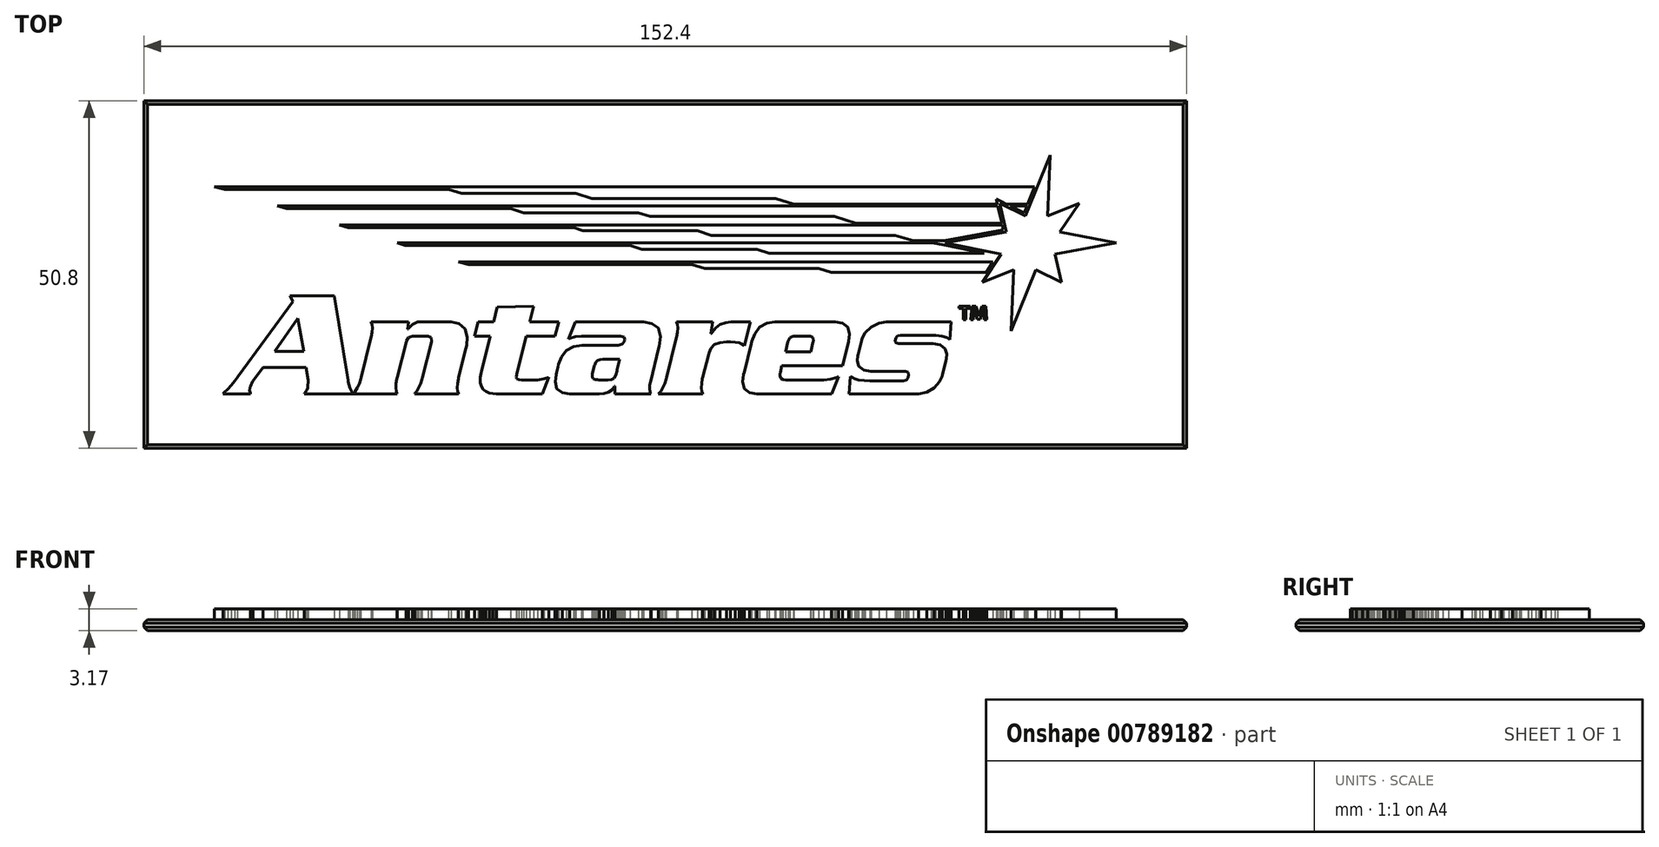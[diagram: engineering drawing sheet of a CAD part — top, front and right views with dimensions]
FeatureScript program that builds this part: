
annotation { "Feature Type Name" : "Feature", "Feature Type Description" : "" }
export const myFeature = defineFeature(function(context is Context, id is Id, definition is map)
    precondition{}
    {
        {
            var Q0;
            Q0=qCreatedBy(makeId("Top.planeOp"),FACE);
            var sketch = newSketch(context, id + "F0", { "sketchPlane" : qUnion([Q0])});
            skLineSegment(sketch, "E0.bottom", {"start": v(76.2, -25.4) * mm, "end": v(-76.2, -25.4) * mm});
            skLineSegment(sketch, "E0.top", {"start": v(76.2, 25.4) * mm, "end": v(-76.2, 25.4) * mm});
            skLineSegment(sketch, "E0.left", {"start": v(76.2, -25.4) * mm, "end": v(76.2, 25.4) * mm});
            skLineSegment(sketch, "E0.right", {"start": v(-76.2, -25.4) * mm, "end": v(-76.2, 25.4) * mm});
            skPoint(sketch, "E0.middle", {"position": v(0, 0) * mm});
            skSolve(sketch);
        }
        {
            var Q0;
            Q0 = qSketchRegion(id + "F0", true);
            extrude(context, id + "F1", {"entities" : qUnion([Q0]), "depth" : 1.59 * mm, "offsetDistance" : 25.4 * mm});
        }
        {
            var Q0;
            Q0=makeQuery(id+"F1.opExtrude","CAP_FACE",FACE,{"disambiguationData":[OSD([sQuery(id+"F0.wireOp",EDGE,"E0.bottom"),sQuery(id+"F0.wireOp",EDGE,"E0.top"),sQuery(id+"F0.wireOp",EDGE,"E0.left"),sQuery(id+"F0.wireOp",EDGE,"E0.right")])],"isStart":false});
            var sketch = newSketch(context, id + "F2", { "sketchPlane" : qUnion([Q0])});
            skLineSegment(sketch, "E1", {"start": v(-52.86, -11.24) * mm, "end": v(-53.7, -6.4) * mm});
            skLineSegment(sketch, "E2", {"start": v(-53.7, -6.4) * mm, "end": v(-57.1, -11.24) * mm});
            skLineSegment(sketch, "E3", {"start": v(-57.1, -11.24) * mm, "end": v(-52.86, -11.24) * mm});
            skLineSegment(sketch, "E4", {"start": v(-58.8, -13.61) * mm, "end": v(-60.26, -15.59) * mm});
            skLineSegment(sketch, "E5", {"start": v(-60.26, -15.59) * mm, "end": v(-60.31, -15.65) * mm});
            skLineSegment(sketch, "E6", {"start": v(-60.31, -15.65) * mm, "end": v(-60.66, -16.36) * mm});
            skLineSegment(sketch, "E7", {"start": v(-60.66, -16.36) * mm, "end": v(-60.68, -16.44) * mm});
            skLineSegment(sketch, "E8", {"start": v(-60.68, -16.44) * mm, "end": v(-60.7, -16.56) * mm});
            skLineSegment(sketch, "E9", {"start": v(-60.7, -16.56) * mm, "end": v(-60.76, -16.95) * mm});
            skLineSegment(sketch, "E10", {"start": v(-60.76, -16.95) * mm, "end": v(-60.66, -17.34) * mm});
            skLineSegment(sketch, "E11", {"start": v(-60.66, -17.34) * mm, "end": v(-60.62, -17.47) * mm});
            skLineSegment(sketch, "E12", {"start": v(-60.62, -17.47) * mm, "end": v(-64.68, -17.47) * mm});
            skLineSegment(sketch, "E13", {"start": v(-64.68, -17.47) * mm, "end": v(-64.5, -17.3) * mm});
            skLineSegment(sketch, "E14", {"start": v(-64.5, -17.3) * mm, "end": v(-63.96, -16.75) * mm});
            skLineSegment(sketch, "E15", {"start": v(-63.96, -16.75) * mm, "end": v(-63.4, -16.17) * mm});
            skLineSegment(sketch, "E16", {"start": v(-63.4, -16.17) * mm, "end": v(-62.92, -15.58) * mm});
            skLineSegment(sketch, "E17", {"start": v(-62.92, -15.58) * mm, "end": v(-62.52, -15.05) * mm});
            skLineSegment(sketch, "E18", {"start": v(-62.52, -15.05) * mm, "end": v(-62.4, -14.87) * mm});
            skLineSegment(sketch, "E19", {"start": v(-62.4, -14.87) * mm, "end": v(-54.45, -3.94) * mm});
            skLineSegment(sketch, "E20", {"start": v(-54.45, -3.94) * mm, "end": v(-54.87, -3.13) * mm});
            skLineSegment(sketch, "E21", {"start": v(-54.87, -3.13) * mm, "end": v(-48.4, -3.13) * mm});
            skLineSegment(sketch, "E22", {"start": v(-48.4, -3.13) * mm, "end": v(-46.37, -15.5) * mm});
            skLineSegment(sketch, "E23", {"start": v(-46.37, -15.5) * mm, "end": v(-46.34, -15.68) * mm});
            skLineSegment(sketch, "E24", {"start": v(-46.34, -15.68) * mm, "end": v(-46.08, -16.56) * mm});
            skLineSegment(sketch, "E25", {"start": v(-46.08, -16.56) * mm, "end": v(-45.7, -17.33) * mm});
            skLineSegment(sketch, "E26", {"start": v(-45.7, -17.33) * mm, "end": v(-45.61, -17.47) * mm});
            skLineSegment(sketch, "E27", {"start": v(-45.61, -17.47) * mm, "end": v(-52.8, -17.47) * mm});
            skLineSegment(sketch, "E28", {"start": v(-52.8, -17.47) * mm, "end": v(-52.7, -17.33) * mm});
            skLineSegment(sketch, "E29", {"start": v(-52.7, -17.33) * mm, "end": v(-52.4, -16.91) * mm});
            skLineSegment(sketch, "E30", {"start": v(-52.4, -16.91) * mm, "end": v(-52.27, -16.6) * mm});
            skLineSegment(sketch, "E31", {"start": v(-52.27, -16.6) * mm, "end": v(-52.25, -16.53) * mm});
            skLineSegment(sketch, "E32", {"start": v(-52.25, -16.53) * mm, "end": v(-52.23, -16.44) * mm});
            skLineSegment(sketch, "E33", {"start": v(-52.23, -16.44) * mm, "end": v(-52.17, -15.53) * mm});
            skLineSegment(sketch, "E34", {"start": v(-52.17, -15.53) * mm, "end": v(-52.19, -15.45) * mm});
            skLineSegment(sketch, "E35", {"start": v(-52.19, -15.45) * mm, "end": v(-52.51, -13.61) * mm});
            skLineSegment(sketch, "E36", {"start": v(-52.51, -13.61) * mm, "end": v(-58.8, -13.61) * mm});
            skLineSegment(sketch, "E37", {"start": v(-37.54, -6.94) * mm, "end": v(-37.66, -8.04) * mm});
            skLineSegment(sketch, "E38", {"start": v(-37.66, -8.04) * mm, "end": v(-37.61, -8.04) * mm});
            skLineSegment(sketch, "E39", {"start": v(-37.61, -8.04) * mm, "end": v(-37.52, -7.9) * mm});
            skLineSegment(sketch, "E40", {"start": v(-37.52, -7.9) * mm, "end": v(-36.95, -7.28) * mm});
            skLineSegment(sketch, "E41", {"start": v(-36.95, -7.28) * mm, "end": v(-36.22, -6.94) * mm});
            skLineSegment(sketch, "E42", {"start": v(-36.22, -6.94) * mm, "end": v(-35.97, -6.94) * mm});
            skLineSegment(sketch, "E43", {"start": v(-35.97, -6.94) * mm, "end": v(-31.7, -6.94) * mm});
            skLineSegment(sketch, "E44", {"start": v(-31.7, -6.94) * mm, "end": v(-31.31, -6.94) * mm});
            skLineSegment(sketch, "E45", {"start": v(-31.31, -6.94) * mm, "end": v(-30.16, -7.2) * mm});
            skLineSegment(sketch, "E46", {"start": v(-30.16, -7.2) * mm, "end": v(-29.26, -7.97) * mm});
            skLineSegment(sketch, "E47", {"start": v(-29.26, -7.97) * mm, "end": v(-28.94, -9.18) * mm});
            skLineSegment(sketch, "E48", {"start": v(-28.94, -9.18) * mm, "end": v(-29.04, -10.38) * mm});
            skLineSegment(sketch, "E49", {"start": v(-29.04, -10.38) * mm, "end": v(-29.13, -10.77) * mm});
            skLineSegment(sketch, "E50", {"start": v(-29.13, -10.77) * mm, "end": v(-30.2, -15.05) * mm});
            skLineSegment(sketch, "E51", {"start": v(-30.2, -15.05) * mm, "end": v(-30.26, -15.27) * mm});
            skLineSegment(sketch, "E52", {"start": v(-30.26, -15.27) * mm, "end": v(-30.38, -15.97) * mm});
            skLineSegment(sketch, "E53", {"start": v(-30.38, -15.97) * mm, "end": v(-30.41, -16.6) * mm});
            skLineSegment(sketch, "E54", {"start": v(-30.41, -16.6) * mm, "end": v(-30.35, -17.07) * mm});
            skLineSegment(sketch, "E55", {"start": v(-30.35, -17.07) * mm, "end": v(-30.25, -17.37) * mm});
            skLineSegment(sketch, "E56", {"start": v(-30.25, -17.37) * mm, "end": v(-30.22, -17.47) * mm});
            skLineSegment(sketch, "E57", {"start": v(-30.22, -17.47) * mm, "end": v(-36.67, -17.47) * mm});
            skLineSegment(sketch, "E58", {"start": v(-36.67, -17.47) * mm, "end": v(-36.6, -17.37) * mm});
            skLineSegment(sketch, "E59", {"start": v(-36.6, -17.37) * mm, "end": v(-36.35, -17.07) * mm});
            skLineSegment(sketch, "E60", {"start": v(-36.35, -17.07) * mm, "end": v(-36.05, -16.6) * mm});
            skLineSegment(sketch, "E61", {"start": v(-36.05, -16.6) * mm, "end": v(-35.76, -15.97) * mm});
            skLineSegment(sketch, "E62", {"start": v(-35.76, -15.97) * mm, "end": v(-35.55, -15.28) * mm});
            skLineSegment(sketch, "E63", {"start": v(-35.55, -15.28) * mm, "end": v(-35.49, -15.05) * mm});
            skLineSegment(sketch, "E64", {"start": v(-35.49, -15.05) * mm, "end": v(-34.2, -9.87) * mm});
            skLineSegment(sketch, "E65", {"start": v(-34.2, -9.87) * mm, "end": v(-34.16, -9.71) * mm});
            skLineSegment(sketch, "E66", {"start": v(-34.16, -9.71) * mm, "end": v(-34.22, -9.2) * mm});
            skLineSegment(sketch, "E67", {"start": v(-34.22, -9.2) * mm, "end": v(-34.7, -9) * mm});
            skLineSegment(sketch, "E68", {"start": v(-34.7, -9) * mm, "end": v(-34.85, -9) * mm});
            skLineSegment(sketch, "E69", {"start": v(-34.85, -9) * mm, "end": v(-36.78, -9) * mm});
            skLineSegment(sketch, "E70", {"start": v(-36.78, -9) * mm, "end": v(-36.96, -9) * mm});
            skLineSegment(sketch, "E71", {"start": v(-36.96, -9) * mm, "end": v(-37.5, -9.2) * mm});
            skLineSegment(sketch, "E72", {"start": v(-37.5, -9.2) * mm, "end": v(-37.83, -9.71) * mm});
            skLineSegment(sketch, "E73", {"start": v(-37.83, -9.71) * mm, "end": v(-37.87, -9.87) * mm});
            skLineSegment(sketch, "E74", {"start": v(-37.87, -9.87) * mm, "end": v(-39.16, -15.05) * mm});
            skLineSegment(sketch, "E75", {"start": v(-39.16, -15.05) * mm, "end": v(-39.22, -15.27) * mm});
            skLineSegment(sketch, "E76", {"start": v(-39.22, -15.27) * mm, "end": v(-39.34, -15.97) * mm});
            skLineSegment(sketch, "E77", {"start": v(-39.34, -15.97) * mm, "end": v(-39.38, -16.6) * mm});
            skLineSegment(sketch, "E78", {"start": v(-39.38, -16.6) * mm, "end": v(-39.3, -17.07) * mm});
            skLineSegment(sketch, "E79", {"start": v(-39.3, -17.07) * mm, "end": v(-39.22, -17.37) * mm});
            skLineSegment(sketch, "E80", {"start": v(-39.22, -17.37) * mm, "end": v(-39.18, -17.47) * mm});
            skLineSegment(sketch, "E81", {"start": v(-39.18, -17.47) * mm, "end": v(-45.64, -17.47) * mm});
            skLineSegment(sketch, "E82", {"start": v(-45.64, -17.47) * mm, "end": v(-45.55, -17.37) * mm});
            skLineSegment(sketch, "E83", {"start": v(-45.55, -17.37) * mm, "end": v(-45.31, -17.07) * mm});
            skLineSegment(sketch, "E84", {"start": v(-45.31, -17.07) * mm, "end": v(-45.01, -16.6) * mm});
            skLineSegment(sketch, "E85", {"start": v(-45.01, -16.6) * mm, "end": v(-44.72, -15.97) * mm});
            skLineSegment(sketch, "E86", {"start": v(-44.72, -15.97) * mm, "end": v(-44.5, -15.28) * mm});
            skLineSegment(sketch, "E87", {"start": v(-44.5, -15.28) * mm, "end": v(-44.45, -15.05) * mm});
            skLineSegment(sketch, "E88", {"start": v(-44.45, -15.05) * mm, "end": v(-43.03, -9.36) * mm});
            skLineSegment(sketch, "E89", {"start": v(-43.03, -9.36) * mm, "end": v(-42.97, -9.13) * mm});
            skLineSegment(sketch, "E90", {"start": v(-42.97, -9.13) * mm, "end": v(-42.85, -8.44) * mm});
            skLineSegment(sketch, "E91", {"start": v(-42.85, -8.44) * mm, "end": v(-42.82, -7.8) * mm});
            skLineSegment(sketch, "E92", {"start": v(-42.82, -7.8) * mm, "end": v(-42.89, -7.34) * mm});
            skLineSegment(sketch, "E93", {"start": v(-42.89, -7.34) * mm, "end": v(-42.98, -7.04) * mm});
            skLineSegment(sketch, "E94", {"start": v(-42.98, -7.04) * mm, "end": v(-43, -6.94) * mm});
            skLineSegment(sketch, "E95", {"start": v(-43, -6.94) * mm, "end": v(-37.54, -6.94) * mm});
            skLineSegment(sketch, "E96", {"start": v(-24.55, -4.79) * mm, "end": v(-19.23, -4.65) * mm});
            skLineSegment(sketch, "E97", {"start": v(-19.23, -4.65) * mm, "end": v(-19.8, -6.94) * mm});
            skLineSegment(sketch, "E98", {"start": v(-19.8, -6.94) * mm, "end": v(-15.59, -6.94) * mm});
            skLineSegment(sketch, "E99", {"start": v(-15.59, -6.94) * mm, "end": v(-16.1, -9) * mm});
            skLineSegment(sketch, "E100", {"start": v(-16.1, -9) * mm, "end": v(-20.31, -9) * mm});
            skLineSegment(sketch, "E101", {"start": v(-20.31, -9) * mm, "end": v(-21.7, -14.56) * mm});
            skLineSegment(sketch, "E102", {"start": v(-21.7, -14.56) * mm, "end": v(-21.72, -14.66) * mm});
            skLineSegment(sketch, "E103", {"start": v(-21.72, -14.66) * mm, "end": v(-21.77, -14.97) * mm});
            skLineSegment(sketch, "E104", {"start": v(-21.77, -14.97) * mm, "end": v(-21.7, -15.23) * mm});
            skLineSegment(sketch, "E105", {"start": v(-21.7, -15.23) * mm, "end": v(-21.41, -15.37) * mm});
            skLineSegment(sketch, "E106", {"start": v(-21.41, -15.37) * mm, "end": v(-21, -15.4) * mm});
            skLineSegment(sketch, "E107", {"start": v(-21, -15.4) * mm, "end": v(-20.86, -15.4) * mm});
            skLineSegment(sketch, "E108", {"start": v(-20.86, -15.4) * mm, "end": v(-19, -15.4) * mm});
            skLineSegment(sketch, "E109", {"start": v(-19, -15.4) * mm, "end": v(-18.68, -15.4) * mm});
            skLineSegment(sketch, "E110", {"start": v(-18.68, -15.4) * mm, "end": v(-17.71, -15.25) * mm});
            skLineSegment(sketch, "E111", {"start": v(-17.71, -15.25) * mm, "end": v(-17.06, -15.03) * mm});
            skLineSegment(sketch, "E112", {"start": v(-17.06, -15.03) * mm, "end": v(-17, -15) * mm});
            skLineSegment(sketch, "E113", {"start": v(-17, -15) * mm, "end": v(-17.94, -17.47) * mm});
            skLineSegment(sketch, "E114", {"start": v(-17.94, -17.47) * mm, "end": v(-24.58, -17.47) * mm});
            skLineSegment(sketch, "E115", {"start": v(-24.58, -17.47) * mm, "end": v(-24.73, -17.47) * mm});
            skLineSegment(sketch, "E116", {"start": v(-24.73, -17.47) * mm, "end": v(-25.19, -17.43) * mm});
            skLineSegment(sketch, "E117", {"start": v(-25.19, -17.43) * mm, "end": v(-25.74, -17.32) * mm});
            skLineSegment(sketch, "E118", {"start": v(-25.74, -17.32) * mm, "end": v(-26.22, -17.12) * mm});
            skLineSegment(sketch, "E119", {"start": v(-26.22, -17.12) * mm, "end": v(-26.6, -16.8) * mm});
            skLineSegment(sketch, "E120", {"start": v(-26.6, -16.8) * mm, "end": v(-26.89, -16.37) * mm});
            skLineSegment(sketch, "E121", {"start": v(-26.89, -16.37) * mm, "end": v(-27.04, -15.8) * mm});
            skLineSegment(sketch, "E122", {"start": v(-27.04, -15.8) * mm, "end": v(-27.05, -15.07) * mm});
            skLineSegment(sketch, "E123", {"start": v(-27.05, -15.07) * mm, "end": v(-26.95, -14.4) * mm});
            skLineSegment(sketch, "E124", {"start": v(-26.95, -14.4) * mm, "end": v(-26.9, -14.18) * mm});
            skLineSegment(sketch, "E125", {"start": v(-26.9, -14.18) * mm, "end": v(-25.6, -9) * mm});
            skLineSegment(sketch, "E126", {"start": v(-25.6, -9) * mm, "end": v(-27.86, -9) * mm});
            skLineSegment(sketch, "E127", {"start": v(-27.86, -9) * mm, "end": v(-27.35, -6.94) * mm});
            skLineSegment(sketch, "E128", {"start": v(-27.35, -6.94) * mm, "end": v(-25.09, -6.94) * mm});
            skLineSegment(sketch, "E129", {"start": v(-25.09, -6.94) * mm, "end": v(-24.55, -4.79) * mm});
            skLineSegment(sketch, "E130", {"start": v(-9, -12.4) * mm, "end": v(-9.13, -12.4) * mm});
            skLineSegment(sketch, "E131", {"start": v(-9.13, -12.4) * mm, "end": v(-9.53, -12.45) * mm});
            skLineSegment(sketch, "E132", {"start": v(-9.53, -12.45) * mm, "end": v(-9.9, -12.58) * mm});
            skLineSegment(sketch, "E133", {"start": v(-9.9, -12.58) * mm, "end": v(-10.17, -12.84) * mm});
            skLineSegment(sketch, "E134", {"start": v(-10.17, -12.84) * mm, "end": v(-10.31, -13.18) * mm});
            skLineSegment(sketch, "E135", {"start": v(-10.31, -13.18) * mm, "end": v(-10.34, -13.3) * mm});
            skLineSegment(sketch, "E136", {"start": v(-10.34, -13.3) * mm, "end": v(-10.64, -14.51) * mm});
            skLineSegment(sketch, "E137", {"start": v(-10.64, -14.51) * mm, "end": v(-10.67, -14.62) * mm});
            skLineSegment(sketch, "E138", {"start": v(-10.67, -14.62) * mm, "end": v(-10.7, -14.97) * mm});
            skLineSegment(sketch, "E139", {"start": v(-10.7, -14.97) * mm, "end": v(-10.57, -15.24) * mm});
            skLineSegment(sketch, "E140", {"start": v(-10.57, -15.24) * mm, "end": v(-10.25, -15.36) * mm});
            skLineSegment(sketch, "E141", {"start": v(-10.25, -15.36) * mm, "end": v(-9.87, -15.4) * mm});
            skLineSegment(sketch, "E142", {"start": v(-9.87, -15.4) * mm, "end": v(-9.75, -15.4) * mm});
            skLineSegment(sketch, "E143", {"start": v(-9.75, -15.4) * mm, "end": v(-8.51, -15.4) * mm});
            skLineSegment(sketch, "E144", {"start": v(-8.51, -15.4) * mm, "end": v(-8.36, -15.4) * mm});
            skLineSegment(sketch, "E145", {"start": v(-8.36, -15.4) * mm, "end": v(-7.9, -15.36) * mm});
            skLineSegment(sketch, "E146", {"start": v(-7.9, -15.36) * mm, "end": v(-7.52, -15.16) * mm});
            skLineSegment(sketch, "E147", {"start": v(-7.52, -15.16) * mm, "end": v(-7.25, -14.7) * mm});
            skLineSegment(sketch, "E148", {"start": v(-7.25, -14.7) * mm, "end": v(-7.07, -14.1) * mm});
            skLineSegment(sketch, "E149", {"start": v(-7.07, -14.1) * mm, "end": v(-7.02, -13.9) * mm});
            skLineSegment(sketch, "E150", {"start": v(-7.02, -13.9) * mm, "end": v(-6.65, -12.4) * mm});
            skLineSegment(sketch, "E151", {"start": v(-6.65, -12.4) * mm, "end": v(-9, -12.4) * mm});
            skLineSegment(sketch, "E152", {"start": v(-3.54, -6.94) * mm, "end": v(-3.14, -6.94) * mm});
            skLineSegment(sketch, "E153", {"start": v(-3.14, -6.94) * mm, "end": v(-1.97, -7.15) * mm});
            skLineSegment(sketch, "E154", {"start": v(-1.97, -7.15) * mm, "end": v(-1.04, -7.84) * mm});
            skLineSegment(sketch, "E155", {"start": v(-1.04, -7.84) * mm, "end": v(-0.72, -9.06) * mm});
            skLineSegment(sketch, "E156", {"start": v(-0.72, -9.06) * mm, "end": v(-0.87, -10.45) * mm});
            skLineSegment(sketch, "E157", {"start": v(-0.87, -10.45) * mm, "end": v(-0.98, -10.9) * mm});
            skLineSegment(sketch, "E158", {"start": v(-0.98, -10.9) * mm, "end": v(-2.13, -15.5) * mm});
            skLineSegment(sketch, "E159", {"start": v(-2.13, -15.5) * mm, "end": v(-2.17, -15.67) * mm});
            skLineSegment(sketch, "E160", {"start": v(-2.17, -15.67) * mm, "end": v(-2.27, -16.2) * mm});
            skLineSegment(sketch, "E161", {"start": v(-2.27, -16.2) * mm, "end": v(-2.3, -16.73) * mm});
            skLineSegment(sketch, "E162", {"start": v(-2.3, -16.73) * mm, "end": v(-2.24, -17.13) * mm});
            skLineSegment(sketch, "E163", {"start": v(-2.24, -17.13) * mm, "end": v(-2.15, -17.39) * mm});
            skLineSegment(sketch, "E164", {"start": v(-2.15, -17.39) * mm, "end": v(-2.1, -17.47) * mm});
            skLineSegment(sketch, "E165", {"start": v(-2.1, -17.47) * mm, "end": v(-7.4, -17.47) * mm});
            skLineSegment(sketch, "E166", {"start": v(-7.4, -17.47) * mm, "end": v(-7.37, -16.3) * mm});
            skLineSegment(sketch, "E167", {"start": v(-7.37, -16.3) * mm, "end": v(-7.42, -16.3) * mm});
            skLineSegment(sketch, "E168", {"start": v(-7.42, -16.3) * mm, "end": v(-7.5, -16.46) * mm});
            skLineSegment(sketch, "E169", {"start": v(-7.5, -16.46) * mm, "end": v(-7.8, -16.88) * mm});
            skLineSegment(sketch, "E170", {"start": v(-7.8, -16.88) * mm, "end": v(-8.29, -17.24) * mm});
            skLineSegment(sketch, "E171", {"start": v(-8.29, -17.24) * mm, "end": v(-8.94, -17.42) * mm});
            skLineSegment(sketch, "E172", {"start": v(-8.94, -17.42) * mm, "end": v(-9.63, -17.47) * mm});
            skLineSegment(sketch, "E173", {"start": v(-9.63, -17.47) * mm, "end": v(-9.86, -17.47) * mm});
            skLineSegment(sketch, "E174", {"start": v(-9.86, -17.47) * mm, "end": v(-13.62, -17.47) * mm});
            skLineSegment(sketch, "E175", {"start": v(-13.62, -17.47) * mm, "end": v(-13.98, -17.47) * mm});
            skLineSegment(sketch, "E176", {"start": v(-13.98, -17.47) * mm, "end": v(-15.05, -17.28) * mm});
            skLineSegment(sketch, "E177", {"start": v(-15.05, -17.28) * mm, "end": v(-15.84, -16.7) * mm});
            skLineSegment(sketch, "E178", {"start": v(-15.84, -16.7) * mm, "end": v(-16.09, -15.71) * mm});
            skLineSegment(sketch, "E179", {"start": v(-16.09, -15.71) * mm, "end": v(-15.96, -14.63) * mm});
            skLineSegment(sketch, "E180", {"start": v(-15.96, -14.63) * mm, "end": v(-15.88, -14.29) * mm});
            skLineSegment(sketch, "E181", {"start": v(-15.88, -14.29) * mm, "end": v(-15.68, -13.52) * mm});
            skLineSegment(sketch, "E182", {"start": v(-15.68, -13.52) * mm, "end": v(-15.6, -13.16) * mm});
            skLineSegment(sketch, "E183", {"start": v(-15.6, -13.16) * mm, "end": v(-15.19, -12.1) * mm});
            skLineSegment(sketch, "E184", {"start": v(-15.19, -12.1) * mm, "end": v(-14.45, -11.11) * mm});
            skLineSegment(sketch, "E185", {"start": v(-14.45, -11.11) * mm, "end": v(-13.37, -10.53) * mm});
            skLineSegment(sketch, "E186", {"start": v(-13.37, -10.53) * mm, "end": v(-12.23, -10.34) * mm});
            skLineSegment(sketch, "E187", {"start": v(-12.23, -10.34) * mm, "end": v(-11.84, -10.34) * mm});
            skLineSegment(sketch, "E188", {"start": v(-11.84, -10.34) * mm, "end": v(-7.03, -10.34) * mm});
            skLineSegment(sketch, "E189", {"start": v(-7.03, -10.34) * mm, "end": v(-6.84, -10.34) * mm});
            skLineSegment(sketch, "E190", {"start": v(-6.84, -10.34) * mm, "end": v(-6.26, -10.2) * mm});
            skLineSegment(sketch, "E191", {"start": v(-6.26, -10.2) * mm, "end": v(-6, -9.8) * mm});
            skLineSegment(sketch, "E192", {"start": v(-6, -9.8) * mm, "end": v(-5.96, -9.67) * mm});
            skLineSegment(sketch, "E193", {"start": v(-5.96, -9.67) * mm, "end": v(-5.94, -9.55) * mm});
            skLineSegment(sketch, "E194", {"start": v(-5.94, -9.55) * mm, "end": v(-6, -9.16) * mm});
            skLineSegment(sketch, "E195", {"start": v(-6, -9.16) * mm, "end": v(-6.52, -9) * mm});
            skLineSegment(sketch, "E196", {"start": v(-6.52, -9) * mm, "end": v(-6.7, -9) * mm});
            skLineSegment(sketch, "E197", {"start": v(-6.7, -9) * mm, "end": v(-11.96, -9) * mm});
            skLineSegment(sketch, "E198", {"start": v(-11.96, -9) * mm, "end": v(-12.26, -9) * mm});
            skLineSegment(sketch, "E199", {"start": v(-12.26, -9) * mm, "end": v(-13.17, -9.1) * mm});
            skLineSegment(sketch, "E200", {"start": v(-13.17, -9.1) * mm, "end": v(-14, -9.37) * mm});
            skLineSegment(sketch, "E201", {"start": v(-14, -9.37) * mm, "end": v(-14.18, -9.45) * mm});
            skLineSegment(sketch, "E202", {"start": v(-14.18, -9.45) * mm, "end": v(-13.17, -6.94) * mm});
            skLineSegment(sketch, "E203", {"start": v(-13.17, -6.94) * mm, "end": v(-3.54, -6.94) * mm});
            skLineSegment(sketch, "E204", {"start": v(6.93, -6.94) * mm, "end": v(6.68, -8.64) * mm});
            skLineSegment(sketch, "E205", {"start": v(6.68, -8.64) * mm, "end": v(6.73, -8.64) * mm});
            skLineSegment(sketch, "E206", {"start": v(6.73, -8.64) * mm, "end": v(6.86, -8.43) * mm});
            skLineSegment(sketch, "E207", {"start": v(6.86, -8.43) * mm, "end": v(7.34, -7.85) * mm});
            skLineSegment(sketch, "E208", {"start": v(7.34, -7.85) * mm, "end": v(7.99, -7.32) * mm});
            skLineSegment(sketch, "E209", {"start": v(7.99, -7.32) * mm, "end": v(8.8, -7.03) * mm});
            skLineSegment(sketch, "E210", {"start": v(8.8, -7.03) * mm, "end": v(9.6, -6.94) * mm});
            skLineSegment(sketch, "E211", {"start": v(9.6, -6.94) * mm, "end": v(9.86, -6.94) * mm});
            skLineSegment(sketch, "E212", {"start": v(9.86, -6.94) * mm, "end": v(12.44, -6.94) * mm});
            skLineSegment(sketch, "E213", {"start": v(12.44, -6.94) * mm, "end": v(11.58, -10.39) * mm});
            skLineSegment(sketch, "E214", {"start": v(11.58, -10.39) * mm, "end": v(11.48, -10.32) * mm});
            skLineSegment(sketch, "E215", {"start": v(11.48, -10.32) * mm, "end": v(11.2, -10.15) * mm});
            skLineSegment(sketch, "E216", {"start": v(11.2, -10.15) * mm, "end": v(10.8, -9.99) * mm});
            skLineSegment(sketch, "E217", {"start": v(10.8, -9.99) * mm, "end": v(10.2, -9.9) * mm});
            skLineSegment(sketch, "E218", {"start": v(10.2, -9.9) * mm, "end": v(9.5, -9.87) * mm});
            skLineSegment(sketch, "E219", {"start": v(9.5, -9.87) * mm, "end": v(9.26, -9.87) * mm});
            skLineSegment(sketch, "E220", {"start": v(9.26, -9.87) * mm, "end": v(8.94, -9.87) * mm});
            skLineSegment(sketch, "E221", {"start": v(8.94, -9.87) * mm, "end": v(7.98, -9.95) * mm});
            skLineSegment(sketch, "E222", {"start": v(7.98, -9.95) * mm, "end": v(7.15, -10.23) * mm});
            skLineSegment(sketch, "E223", {"start": v(7.15, -10.23) * mm, "end": v(6.65, -10.78) * mm});
            skLineSegment(sketch, "E224", {"start": v(6.65, -10.78) * mm, "end": v(6.39, -11.44) * mm});
            skLineSegment(sketch, "E225", {"start": v(6.39, -11.44) * mm, "end": v(6.33, -11.67) * mm});
            skLineSegment(sketch, "E226", {"start": v(6.33, -11.67) * mm, "end": v(5.49, -15.05) * mm});
            skLineSegment(sketch, "E227", {"start": v(5.49, -15.05) * mm, "end": v(5.43, -15.27) * mm});
            skLineSegment(sketch, "E228", {"start": v(5.43, -15.27) * mm, "end": v(5.3, -15.97) * mm});
            skLineSegment(sketch, "E229", {"start": v(5.3, -15.97) * mm, "end": v(5.27, -16.6) * mm});
            skLineSegment(sketch, "E230", {"start": v(5.27, -16.6) * mm, "end": v(5.34, -17.07) * mm});
            skLineSegment(sketch, "E231", {"start": v(5.34, -17.07) * mm, "end": v(5.43, -17.37) * mm});
            skLineSegment(sketch, "E232", {"start": v(5.43, -17.37) * mm, "end": v(5.47, -17.47) * mm});
            skLineSegment(sketch, "E233", {"start": v(5.47, -17.47) * mm, "end": v(-0.99, -17.47) * mm});
            skLineSegment(sketch, "E234", {"start": v(-0.99, -17.47) * mm, "end": v(-0.9, -17.37) * mm});
            skLineSegment(sketch, "E235", {"start": v(-0.9, -17.37) * mm, "end": v(-0.66, -17.07) * mm});
            skLineSegment(sketch, "E236", {"start": v(-0.66, -17.07) * mm, "end": v(-0.36, -16.6) * mm});
            skLineSegment(sketch, "E237", {"start": v(-0.36, -16.6) * mm, "end": v(-0.08, -15.97) * mm});
            skLineSegment(sketch, "E238", {"start": v(-0.08, -15.97) * mm, "end": v(0.14, -15.28) * mm});
            skLineSegment(sketch, "E239", {"start": v(0.14, -15.28) * mm, "end": v(0.2, -15.05) * mm});
            skLineSegment(sketch, "E240", {"start": v(0.2, -15.05) * mm, "end": v(1.62, -9.36) * mm});
            skLineSegment(sketch, "E241", {"start": v(1.62, -9.36) * mm, "end": v(1.67, -9.13) * mm});
            skLineSegment(sketch, "E242", {"start": v(1.67, -9.13) * mm, "end": v(1.8, -8.44) * mm});
            skLineSegment(sketch, "E243", {"start": v(1.8, -8.44) * mm, "end": v(1.83, -7.8) * mm});
            skLineSegment(sketch, "E244", {"start": v(1.83, -7.8) * mm, "end": v(1.76, -7.34) * mm});
            skLineSegment(sketch, "E245", {"start": v(1.76, -7.34) * mm, "end": v(1.67, -7.04) * mm});
            skLineSegment(sketch, "E246", {"start": v(1.67, -7.04) * mm, "end": v(1.64, -6.94) * mm});
            skLineSegment(sketch, "E247", {"start": v(1.64, -6.94) * mm, "end": v(6.93, -6.94) * mm});
            skLineSegment(sketch, "E248", {"start": v(21.25, -11.29) * mm, "end": v(21.61, -9.85) * mm});
            skLineSegment(sketch, "E249", {"start": v(21.61, -9.85) * mm, "end": v(21.65, -9.7) * mm});
            skLineSegment(sketch, "E250", {"start": v(21.65, -9.7) * mm, "end": v(21.61, -9.2) * mm});
            skLineSegment(sketch, "E251", {"start": v(21.61, -9.2) * mm, "end": v(21.2, -9) * mm});
            skLineSegment(sketch, "E252", {"start": v(21.2, -9) * mm, "end": v(21.06, -9) * mm});
            skLineSegment(sketch, "E253", {"start": v(21.06, -9) * mm, "end": v(18.9, -9) * mm});
            skLineSegment(sketch, "E254", {"start": v(18.9, -9) * mm, "end": v(18.73, -9) * mm});
            skLineSegment(sketch, "E255", {"start": v(18.73, -9) * mm, "end": v(18.24, -9.2) * mm});
            skLineSegment(sketch, "E256", {"start": v(18.24, -9.2) * mm, "end": v(17.95, -9.7) * mm});
            skLineSegment(sketch, "E257", {"start": v(17.95, -9.7) * mm, "end": v(17.92, -9.85) * mm});
            skLineSegment(sketch, "E258", {"start": v(17.92, -9.85) * mm, "end": v(17.56, -11.29) * mm});
            skLineSegment(sketch, "E259", {"start": v(17.56, -11.29) * mm, "end": v(21.25, -11.29) * mm});
            skLineSegment(sketch, "E260", {"start": v(17.04, -13.35) * mm, "end": v(16.8, -14.33) * mm});
            skLineSegment(sketch, "E261", {"start": v(16.8, -14.33) * mm, "end": v(16.77, -14.45) * mm});
            skLineSegment(sketch, "E262", {"start": v(16.77, -14.45) * mm, "end": v(16.75, -14.82) * mm});
            skLineSegment(sketch, "E263", {"start": v(16.75, -14.82) * mm, "end": v(16.89, -15.15) * mm});
            skLineSegment(sketch, "E264", {"start": v(16.89, -15.15) * mm, "end": v(17.21, -15.35) * mm});
            skLineSegment(sketch, "E265", {"start": v(17.21, -15.35) * mm, "end": v(17.6, -15.4) * mm});
            skLineSegment(sketch, "E266", {"start": v(17.6, -15.4) * mm, "end": v(17.74, -15.4) * mm});
            skLineSegment(sketch, "E267", {"start": v(17.74, -15.4) * mm, "end": v(22.83, -15.4) * mm});
            skLineSegment(sketch, "E268", {"start": v(22.83, -15.4) * mm, "end": v(23.14, -15.4) * mm});
            skLineSegment(sketch, "E269", {"start": v(23.14, -15.4) * mm, "end": v(24.1, -15.33) * mm});
            skLineSegment(sketch, "E270", {"start": v(24.1, -15.33) * mm, "end": v(25.1, -15.05) * mm});
            skLineSegment(sketch, "E271", {"start": v(25.1, -15.05) * mm, "end": v(25.34, -14.96) * mm});
            skLineSegment(sketch, "E272", {"start": v(25.34, -14.96) * mm, "end": v(24.3, -17.47) * mm});
            skLineSegment(sketch, "E273", {"start": v(24.3, -17.47) * mm, "end": v(13.78, -17.47) * mm});
            skLineSegment(sketch, "E274", {"start": v(13.78, -17.47) * mm, "end": v(13.42, -17.47) * mm});
            skLineSegment(sketch, "E275", {"start": v(13.42, -17.47) * mm, "end": v(12.34, -17.28) * mm});
            skLineSegment(sketch, "E276", {"start": v(12.34, -17.28) * mm, "end": v(11.55, -16.7) * mm});
            skLineSegment(sketch, "E277", {"start": v(11.55, -16.7) * mm, "end": v(11.3, -15.7) * mm});
            skLineSegment(sketch, "E278", {"start": v(11.3, -15.7) * mm, "end": v(11.44, -14.63) * mm});
            skLineSegment(sketch, "E279", {"start": v(11.44, -14.63) * mm, "end": v(11.52, -14.29) * mm});
            skLineSegment(sketch, "E280", {"start": v(11.52, -14.29) * mm, "end": v(12.56, -10.12) * mm});
            skLineSegment(sketch, "E281", {"start": v(12.56, -10.12) * mm, "end": v(12.65, -9.75) * mm});
            skLineSegment(sketch, "E282", {"start": v(12.65, -9.75) * mm, "end": v(13.06, -8.7) * mm});
            skLineSegment(sketch, "E283", {"start": v(13.06, -8.7) * mm, "end": v(13.8, -7.7) * mm});
            skLineSegment(sketch, "E284", {"start": v(13.8, -7.7) * mm, "end": v(14.88, -7.13) * mm});
            skLineSegment(sketch, "E285", {"start": v(14.88, -7.13) * mm, "end": v(16.02, -6.94) * mm});
            skLineSegment(sketch, "E286", {"start": v(16.02, -6.94) * mm, "end": v(16.4, -6.94) * mm});
            skLineSegment(sketch, "E287", {"start": v(16.4, -6.94) * mm, "end": v(24.45, -6.94) * mm});
            skLineSegment(sketch, "E288", {"start": v(24.45, -6.94) * mm, "end": v(24.8, -6.94) * mm});
            skLineSegment(sketch, "E289", {"start": v(24.8, -6.94) * mm, "end": v(25.88, -7.13) * mm});
            skLineSegment(sketch, "E290", {"start": v(25.88, -7.13) * mm, "end": v(26.67, -7.7) * mm});
            skLineSegment(sketch, "E291", {"start": v(26.67, -7.7) * mm, "end": v(26.91, -8.7) * mm});
            skLineSegment(sketch, "E292", {"start": v(26.91, -8.7) * mm, "end": v(26.78, -9.77) * mm});
            skLineSegment(sketch, "E293", {"start": v(26.78, -9.77) * mm, "end": v(26.7, -10.12) * mm});
            skLineSegment(sketch, "E294", {"start": v(26.7, -10.12) * mm, "end": v(25.9, -13.35) * mm});
            skLineSegment(sketch, "E295", {"start": v(25.9, -13.35) * mm, "end": v(17.04, -13.35) * mm});
            skLineSegment(sketch, "E296", {"start": v(38.78, -10.08) * mm, "end": v(39.14, -10.08) * mm});
            skLineSegment(sketch, "E297", {"start": v(39.14, -10.08) * mm, "end": v(40.2, -10.29) * mm});
            skLineSegment(sketch, "E298", {"start": v(40.2, -10.29) * mm, "end": v(40.9, -10.85) * mm});
            skLineSegment(sketch, "E299", {"start": v(40.9, -10.85) * mm, "end": v(41.12, -11.65) * mm});
            skLineSegment(sketch, "E300", {"start": v(41.12, -11.65) * mm, "end": v(41.07, -12.35) * mm});
            skLineSegment(sketch, "E301", {"start": v(41.07, -12.35) * mm, "end": v(41.03, -12.58) * mm});
            skLineSegment(sketch, "E302", {"start": v(41.03, -12.58) * mm, "end": v(40.5, -14.7) * mm});
            skLineSegment(sketch, "E303", {"start": v(40.5, -14.7) * mm, "end": v(40.44, -14.95) * mm});
            skLineSegment(sketch, "E304", {"start": v(40.44, -14.95) * mm, "end": v(40.09, -15.7) * mm});
            skLineSegment(sketch, "E305", {"start": v(40.09, -15.7) * mm, "end": v(39.33, -16.58) * mm});
            skLineSegment(sketch, "E306", {"start": v(39.33, -16.58) * mm, "end": v(38.2, -17.22) * mm});
            skLineSegment(sketch, "E307", {"start": v(38.2, -17.22) * mm, "end": v(37.03, -17.47) * mm});
            skLineSegment(sketch, "E308", {"start": v(37.03, -17.47) * mm, "end": v(36.65, -17.47) * mm});
            skLineSegment(sketch, "E309", {"start": v(36.65, -17.47) * mm, "end": v(26.84, -17.47) * mm});
            skLineSegment(sketch, "E310", {"start": v(26.84, -17.47) * mm, "end": v(27.06, -14.94) * mm});
            skLineSegment(sketch, "E311", {"start": v(27.06, -14.94) * mm, "end": v(27.2, -15.01) * mm});
            skLineSegment(sketch, "E312", {"start": v(27.2, -15.01) * mm, "end": v(27.65, -15.22) * mm});
            skLineSegment(sketch, "E313", {"start": v(27.65, -15.22) * mm, "end": v(28.26, -15.4) * mm});
            skLineSegment(sketch, "E314", {"start": v(28.26, -15.4) * mm, "end": v(29.05, -15.5) * mm});
            skLineSegment(sketch, "E315", {"start": v(29.05, -15.5) * mm, "end": v(29.92, -15.54) * mm});
            skLineSegment(sketch, "E316", {"start": v(29.92, -15.54) * mm, "end": v(30.2, -15.54) * mm});
            skLineSegment(sketch, "E317", {"start": v(30.2, -15.54) * mm, "end": v(34.67, -15.54) * mm});
            skLineSegment(sketch, "E318", {"start": v(34.67, -15.54) * mm, "end": v(34.8, -15.54) * mm});
            skLineSegment(sketch, "E319", {"start": v(34.8, -15.54) * mm, "end": v(35.24, -15.42) * mm});
            skLineSegment(sketch, "E320", {"start": v(35.24, -15.42) * mm, "end": v(35.47, -15.09) * mm});
            skLineSegment(sketch, "E321", {"start": v(35.47, -15.09) * mm, "end": v(35.5, -14.98) * mm});
            skLineSegment(sketch, "E322", {"start": v(35.5, -14.98) * mm, "end": v(35.56, -14.76) * mm});
            skLineSegment(sketch, "E323", {"start": v(35.56, -14.76) * mm, "end": v(35.58, -14.65) * mm});
            skLineSegment(sketch, "E324", {"start": v(35.58, -14.65) * mm, "end": v(35.52, -14.32) * mm});
            skLineSegment(sketch, "E325", {"start": v(35.52, -14.32) * mm, "end": v(35.13, -14.2) * mm});
            skLineSegment(sketch, "E326", {"start": v(35.13, -14.2) * mm, "end": v(35, -14.2) * mm});
            skLineSegment(sketch, "E327", {"start": v(35, -14.2) * mm, "end": v(30.4, -14.2) * mm});
            skLineSegment(sketch, "E328", {"start": v(30.4, -14.2) * mm, "end": v(30.05, -14.2) * mm});
            skLineSegment(sketch, "E329", {"start": v(30.05, -14.2) * mm, "end": v(29, -13.98) * mm});
            skLineSegment(sketch, "E330", {"start": v(29, -13.98) * mm, "end": v(28.29, -13.42) * mm});
            skLineSegment(sketch, "E331", {"start": v(28.29, -13.42) * mm, "end": v(28.07, -12.6) * mm});
            skLineSegment(sketch, "E332", {"start": v(28.07, -12.6) * mm, "end": v(28.13, -11.9) * mm});
            skLineSegment(sketch, "E333", {"start": v(28.13, -11.9) * mm, "end": v(28.17, -11.67) * mm});
            skLineSegment(sketch, "E334", {"start": v(28.17, -11.67) * mm, "end": v(28.68, -9.63) * mm});
            skLineSegment(sketch, "E335", {"start": v(28.68, -9.63) * mm, "end": v(28.75, -9.34) * mm});
            skLineSegment(sketch, "E336", {"start": v(28.75, -9.34) * mm, "end": v(29.2, -8.53) * mm});
            skLineSegment(sketch, "E337", {"start": v(29.2, -8.53) * mm, "end": v(30.08, -7.68) * mm});
            skLineSegment(sketch, "E338", {"start": v(30.08, -7.68) * mm, "end": v(31.27, -7.13) * mm});
            skLineSegment(sketch, "E339", {"start": v(31.27, -7.13) * mm, "end": v(32.33, -6.94) * mm});
            skLineSegment(sketch, "E340", {"start": v(32.33, -6.94) * mm, "end": v(32.69, -6.94) * mm});
            skLineSegment(sketch, "E341", {"start": v(32.69, -6.94) * mm, "end": v(41.78, -6.94) * mm});
            skLineSegment(sketch, "E342", {"start": v(41.78, -6.94) * mm, "end": v(41.58, -9.56) * mm});
            skLineSegment(sketch, "E343", {"start": v(41.58, -9.56) * mm, "end": v(41.52, -9.45) * mm});
            skLineSegment(sketch, "E344", {"start": v(41.52, -9.45) * mm, "end": v(41.16, -9.23) * mm});
            skLineSegment(sketch, "E345", {"start": v(41.16, -9.23) * mm, "end": v(40.45, -9.02) * mm});
            skLineSegment(sketch, "E346", {"start": v(40.45, -9.02) * mm, "end": v(39.56, -8.9) * mm});
            skLineSegment(sketch, "E347", {"start": v(39.56, -8.9) * mm, "end": v(38.85, -8.87) * mm});
            skLineSegment(sketch, "E348", {"start": v(38.85, -8.87) * mm, "end": v(38.62, -8.87) * mm});
            skLineSegment(sketch, "E349", {"start": v(38.62, -8.87) * mm, "end": v(34.52, -8.87) * mm});
            skLineSegment(sketch, "E350", {"start": v(34.52, -8.87) * mm, "end": v(34.37, -8.87) * mm});
            skLineSegment(sketch, "E351", {"start": v(34.37, -8.87) * mm, "end": v(33.94, -8.96) * mm});
            skLineSegment(sketch, "E352", {"start": v(33.94, -8.96) * mm, "end": v(33.72, -9.18) * mm});
            skLineSegment(sketch, "E353", {"start": v(33.72, -9.18) * mm, "end": v(33.7, -9.25) * mm});
            skLineSegment(sketch, "E354", {"start": v(33.7, -9.25) * mm, "end": v(33.6, -9.7) * mm});
            skLineSegment(sketch, "E355", {"start": v(33.6, -9.7) * mm, "end": v(33.58, -9.75) * mm});
            skLineSegment(sketch, "E356", {"start": v(33.58, -9.75) * mm, "end": v(33.69, -9.98) * mm});
            skLineSegment(sketch, "E357", {"start": v(33.69, -9.98) * mm, "end": v(34.08, -10.08) * mm});
            skLineSegment(sketch, "E358", {"start": v(34.08, -10.08) * mm, "end": v(34.21, -10.08) * mm});
            skLineSegment(sketch, "E359", {"start": v(34.21, -10.08) * mm, "end": v(38.78, -10.08) * mm});
            skLineSegment(sketch, "E360", {"start": v(-29.78, 11.88) * mm, "end": v(-13.1, 11.88) * mm});
            skLineSegment(sketch, "E361", {"start": v(-13.1, 11.88) * mm, "end": v(-10.71, 11.13) * mm});
            skLineSegment(sketch, "E362", {"start": v(-10.71, 11.13) * mm, "end": v(16.12, 11.13) * mm});
            skLineSegment(sketch, "E363", {"start": v(16.12, 11.13) * mm, "end": v(18.82, 10.3) * mm});
            skLineSegment(sketch, "E364", {"start": v(18.82, 10.3) * mm, "end": v(48.53, 10.3) * mm});
            skLineSegment(sketch, "E365", {"start": v(48.53, 10.3) * mm, "end": v(48.52, 10.32) * mm});
            skLineSegment(sketch, "E366", {"start": v(48.52, 10.32) * mm, "end": v(48.35, 11.04) * mm});
            skLineSegment(sketch, "E367", {"start": v(48.35, 11.04) * mm, "end": v(49.01, 10.72) * mm});
            skLineSegment(sketch, "E368", {"start": v(49.01, 10.72) * mm, "end": v(49.86, 10.3) * mm});
            skLineSegment(sketch, "E369", {"start": v(49.86, 10.3) * mm, "end": v(52.99, 10.3) * mm});
            skLineSegment(sketch, "E370", {"start": v(52.99, 10.3) * mm, "end": v(54, 12.8) * mm});
            skLineSegment(sketch, "E371", {"start": v(54, 12.8) * mm, "end": v(-65.94, 12.8) * mm});
            skLineSegment(sketch, "E372", {"start": v(-65.94, 12.8) * mm, "end": v(-64.42, 12.44) * mm});
            skLineSegment(sketch, "E373", {"start": v(-64.42, 12.44) * mm, "end": v(-31.66, 12.44) * mm});
            skLineSegment(sketch, "E374", {"start": v(-31.66, 12.44) * mm, "end": v(-29.78, 11.88) * mm});
            skLineSegment(sketch, "E375", {"start": v(52.47, 9.02) * mm, "end": v(52.87, 10.02) * mm});
            skLineSegment(sketch, "E376", {"start": v(52.87, 10.02) * mm, "end": v(50.44, 10.02) * mm});
            skLineSegment(sketch, "E377", {"start": v(50.44, 10.02) * mm, "end": v(52.47, 9.02) * mm});
            skLineSegment(sketch, "E378", {"start": v(47.9, 1.83) * mm, "end": v(-30.2, 1.83) * mm});
            skLineSegment(sketch, "E379", {"start": v(-30.2, 1.83) * mm, "end": v(-28.75, 1.46) * mm});
            skLineSegment(sketch, "E380", {"start": v(-28.75, 1.46) * mm, "end": v(3.9, 1.46) * mm});
            skLineSegment(sketch, "E381", {"start": v(3.9, 1.46) * mm, "end": v(5.8, 0.9) * mm});
            skLineSegment(sketch, "E382", {"start": v(5.8, 0.9) * mm, "end": v(22.39, 0.9) * mm});
            skLineSegment(sketch, "E383", {"start": v(22.39, 0.9) * mm, "end": v(24.25, 0.34) * mm});
            skLineSegment(sketch, "E384", {"start": v(24.25, 0.34) * mm, "end": v(46.9, 0.34) * mm});
            skLineSegment(sketch, "E385", {"start": v(46.9, 0.34) * mm, "end": v(47.9, 1.83) * mm});
            skLineSegment(sketch, "E386", {"start": v(-20.7, 9.04) * mm, "end": v(-3.91, 9.04) * mm});
            skLineSegment(sketch, "E387", {"start": v(-3.91, 9.04) * mm, "end": v(-2.24, 8.53) * mm});
            skLineSegment(sketch, "E388", {"start": v(-2.24, 8.53) * mm, "end": v(24.69, 8.53) * mm});
            skLineSegment(sketch, "E389", {"start": v(24.69, 8.53) * mm, "end": v(27.86, 7.5) * mm});
            skLineSegment(sketch, "E390", {"start": v(27.86, 7.5) * mm, "end": v(49.18, 7.5) * mm});
            skLineSegment(sketch, "E391", {"start": v(49.18, 7.5) * mm, "end": v(48.6, 10.02) * mm});
            skLineSegment(sketch, "E392", {"start": v(48.6, 10.02) * mm, "end": v(-56.73, 10.02) * mm});
            skLineSegment(sketch, "E393", {"start": v(-56.73, 10.02) * mm, "end": v(-55.39, 9.65) * mm});
            skLineSegment(sketch, "E394", {"start": v(-55.39, 9.65) * mm, "end": v(-22.61, 9.65) * mm});
            skLineSegment(sketch, "E395", {"start": v(-22.61, 9.65) * mm, "end": v(-20.7, 9.04) * mm});
            skLineSegment(sketch, "E396", {"start": v(-3.4, 3.69) * mm, "end": v(13.4, 3.69) * mm});
            skLineSegment(sketch, "E397", {"start": v(13.4, 3.69) * mm, "end": v(15.2, 3.13) * mm});
            skLineSegment(sketch, "E398", {"start": v(15.2, 3.13) * mm, "end": v(46.63, 3.13) * mm});
            skLineSegment(sketch, "E399", {"start": v(46.63, 3.13) * mm, "end": v(40.8, 4.28) * mm});
            skLineSegment(sketch, "E400", {"start": v(40.8, 4.28) * mm, "end": v(39.07, 4.62) * mm});
            skLineSegment(sketch, "E401", {"start": v(39.07, 4.62) * mm, "end": v(-39.2, 4.62) * mm});
            skLineSegment(sketch, "E402", {"start": v(-39.2, 4.62) * mm, "end": v(-38.05, 4.25) * mm});
            skLineSegment(sketch, "E403", {"start": v(-38.05, 4.25) * mm, "end": v(-5.14, 4.25) * mm});
            skLineSegment(sketch, "E404", {"start": v(-5.14, 4.25) * mm, "end": v(-3.4, 3.69) * mm});
            skLineSegment(sketch, "E405", {"start": v(-12.04, 6.39) * mm, "end": v(4.67, 6.39) * mm});
            skLineSegment(sketch, "E406", {"start": v(4.67, 6.39) * mm, "end": v(6.75, 5.74) * mm});
            skLineSegment(sketch, "E407", {"start": v(6.75, 5.74) * mm, "end": v(33.59, 5.74) * mm});
            skLineSegment(sketch, "E408", {"start": v(33.59, 5.74) * mm, "end": v(36.26, 4.92) * mm});
            skLineSegment(sketch, "E409", {"start": v(36.26, 4.92) * mm, "end": v(40.57, 4.92) * mm});
            skLineSegment(sketch, "E410", {"start": v(40.57, 4.92) * mm, "end": v(40.8, 4.96) * mm});
            skLineSegment(sketch, "E411", {"start": v(40.8, 4.96) * mm, "end": v(49.42, 6.52) * mm});
            skLineSegment(sketch, "E412", {"start": v(49.42, 6.52) * mm, "end": v(49.25, 7.23) * mm});
            skLineSegment(sketch, "E413", {"start": v(49.25, 7.23) * mm, "end": v(-47.6, 7.23) * mm});
            skLineSegment(sketch, "E414", {"start": v(-47.6, 7.23) * mm, "end": v(-46.37, 6.85) * mm});
            skLineSegment(sketch, "E415", {"start": v(-46.37, 6.85) * mm, "end": v(-13.33, 6.83) * mm});
            skLineSegment(sketch, "E416", {"start": v(-13.33, 6.83) * mm, "end": v(-12.04, 6.39) * mm});
            skLineSegment(sketch, "E417", {"start": v(57.69, 6.25) * mm, "end": v(60.52, 10.4) * mm});
            skLineSegment(sketch, "E418", {"start": v(60.52, 10.4) * mm, "end": v(55.9, 8.55) * mm});
            skLineSegment(sketch, "E419", {"start": v(55.9, 8.55) * mm, "end": v(56.27, 17.47) * mm});
            skLineSegment(sketch, "E420", {"start": v(56.27, 17.47) * mm, "end": v(52.65, 8.55) * mm});
            skLineSegment(sketch, "E421", {"start": v(52.65, 8.55) * mm, "end": v(48.86, 10.4) * mm});
            skLineSegment(sketch, "E422", {"start": v(48.86, 10.4) * mm, "end": v(49.84, 6.25) * mm});
            skLineSegment(sketch, "E423", {"start": v(49.84, 6.25) * mm, "end": v(40.86, 4.62) * mm});
            skLineSegment(sketch, "E424", {"start": v(40.86, 4.62) * mm, "end": v(49.11, 3) * mm});
            skLineSegment(sketch, "E425", {"start": v(49.11, 3) * mm, "end": v(46.34, -1.13) * mm});
            skLineSegment(sketch, "E426", {"start": v(46.34, -1.13) * mm, "end": v(50.9, 0.7) * mm});
            skLineSegment(sketch, "E427", {"start": v(50.9, 0.7) * mm, "end": v(50.53, -8.23) * mm});
            skLineSegment(sketch, "E428", {"start": v(50.53, -8.23) * mm, "end": v(54.15, 0.7) * mm});
            skLineSegment(sketch, "E429", {"start": v(54.15, 0.7) * mm, "end": v(57.9, -1.13) * mm});
            skLineSegment(sketch, "E430", {"start": v(57.9, -1.13) * mm, "end": v(56.96, 3) * mm});
            skLineSegment(sketch, "E431", {"start": v(56.96, 3) * mm, "end": v(65.94, 4.62) * mm});
            skLineSegment(sketch, "E432", {"start": v(65.94, 4.62) * mm, "end": v(57.69, 6.25) * mm});
            skLineSegment(sketch, "E433", {"start": v(46.63, -6.58) * mm, "end": v(46.56, -5.45) * mm});
            skLineSegment(sketch, "E434", {"start": v(46.56, -5.45) * mm, "end": v(46.55, -5.4) * mm});
            skLineSegment(sketch, "E435", {"start": v(46.55, -5.4) * mm, "end": v(46.54, -4.96) * mm});
            skLineSegment(sketch, "E436", {"start": v(46.54, -4.96) * mm, "end": v(46.54, -4.9) * mm});
            skLineSegment(sketch, "E437", {"start": v(46.54, -4.9) * mm, "end": v(46.52, -4.9) * mm});
            skLineSegment(sketch, "E438", {"start": v(46.52, -4.9) * mm, "end": v(46.5, -4.95) * mm});
            skLineSegment(sketch, "E439", {"start": v(46.5, -4.95) * mm, "end": v(46.37, -5.44) * mm});
            skLineSegment(sketch, "E440", {"start": v(46.37, -5.44) * mm, "end": v(46.36, -5.48) * mm});
            skLineSegment(sketch, "E441", {"start": v(46.36, -5.48) * mm, "end": v(46.01, -6.55) * mm});
            skLineSegment(sketch, "E442", {"start": v(46.01, -6.55) * mm, "end": v(45.61, -6.55) * mm});
            skLineSegment(sketch, "E443", {"start": v(45.61, -6.55) * mm, "end": v(45.27, -5.45) * mm});
            skLineSegment(sketch, "E444", {"start": v(45.27, -5.45) * mm, "end": v(45.26, -5.42) * mm});
            skLineSegment(sketch, "E445", {"start": v(45.26, -5.42) * mm, "end": v(45.14, -4.95) * mm});
            skLineSegment(sketch, "E446", {"start": v(45.14, -4.95) * mm, "end": v(45.13, -4.9) * mm});
            skLineSegment(sketch, "E447", {"start": v(45.13, -4.9) * mm, "end": v(45.11, -4.9) * mm});
            skLineSegment(sketch, "E448", {"start": v(45.11, -4.9) * mm, "end": v(45.11, -5.04) * mm});
            skLineSegment(sketch, "E449", {"start": v(45.11, -5.04) * mm, "end": v(45.1, -5.4) * mm});
            skLineSegment(sketch, "E450", {"start": v(45.1, -5.4) * mm, "end": v(45.1, -5.45) * mm});
            skLineSegment(sketch, "E451", {"start": v(45.1, -5.45) * mm, "end": v(45.03, -6.58) * mm});
            skLineSegment(sketch, "E452", {"start": v(45.03, -6.58) * mm, "end": v(44.66, -6.58) * mm});
            skLineSegment(sketch, "E453", {"start": v(44.66, -6.58) * mm, "end": v(44.8, -4.65) * mm});
            skLineSegment(sketch, "E454", {"start": v(44.8, -4.65) * mm, "end": v(45.37, -4.65) * mm});
            skLineSegment(sketch, "E455", {"start": v(45.37, -4.65) * mm, "end": v(45.7, -5.6) * mm});
            skLineSegment(sketch, "E456", {"start": v(45.7, -5.6) * mm, "end": v(45.72, -5.63) * mm});
            skLineSegment(sketch, "E457", {"start": v(45.72, -5.63) * mm, "end": v(45.82, -6.04) * mm});
            skLineSegment(sketch, "E458", {"start": v(45.82, -6.04) * mm, "end": v(45.83, -6.09) * mm});
            skLineSegment(sketch, "E459", {"start": v(45.83, -6.09) * mm, "end": v(45.84, -6.09) * mm});
            skLineSegment(sketch, "E460", {"start": v(45.84, -6.09) * mm, "end": v(45.85, -6.04) * mm});
            skLineSegment(sketch, "E461", {"start": v(45.85, -6.04) * mm, "end": v(45.96, -5.64) * mm});
            skLineSegment(sketch, "E462", {"start": v(45.96, -5.64) * mm, "end": v(45.98, -5.61) * mm});
            skLineSegment(sketch, "E463", {"start": v(45.98, -5.61) * mm, "end": v(46.3, -4.65) * mm});
            skLineSegment(sketch, "E464", {"start": v(46.3, -4.65) * mm, "end": v(46.86, -4.65) * mm});
            skLineSegment(sketch, "E465", {"start": v(46.86, -4.65) * mm, "end": v(47.01, -6.58) * mm});
            skLineSegment(sketch, "E466", {"start": v(47.01, -6.58) * mm, "end": v(46.63, -6.58) * mm});
            skLineSegment(sketch, "E467", {"start": v(44.54, -4.65) * mm, "end": v(44.54, -4.97) * mm});
            skLineSegment(sketch, "E468", {"start": v(44.54, -4.97) * mm, "end": v(43.93, -4.97) * mm});
            skLineSegment(sketch, "E469", {"start": v(43.93, -4.97) * mm, "end": v(43.93, -6.58) * mm});
            skLineSegment(sketch, "E470", {"start": v(43.93, -6.58) * mm, "end": v(43.54, -6.58) * mm});
            skLineSegment(sketch, "E471", {"start": v(43.54, -6.58) * mm, "end": v(43.54, -4.97) * mm});
            skLineSegment(sketch, "E472", {"start": v(43.54, -4.97) * mm, "end": v(42.93, -4.97) * mm});
            skLineSegment(sketch, "E473", {"start": v(42.93, -4.97) * mm, "end": v(42.93, -4.65) * mm});
            skLineSegment(sketch, "E474", {"start": v(42.93, -4.65) * mm, "end": v(44.54, -4.65) * mm});
            skSolve(sketch);
        }
        {
            var Q0;
            Q0=makeQuery(id+"F2.imprint","IMPRINT",FACE,{"disambiguationData":[TD([[makeQuery(id+"F2.imprint","IMPRINT",EDGE,{"derivedFrom":sQuery(id+"F2.wireOp",EDGE,"E130")}),-1.0]])]});
            var Q1;
            Q1=makeQuery(id+"F2.imprint","IMPRINT",FACE,{"disambiguationData":[TD([[makeQuery(id+"F2.imprint","IMPRINT",EDGE,{"derivedFrom":sQuery(id+"F2.wireOp",EDGE,"E248")}),-1.0]])]});
            var Q2;
            Q2=makeQuery(id+"F2.imprint","IMPRINT",FACE,{"disambiguationData":[TD([[makeQuery(id+"F2.imprint","IMPRINT",EDGE,{"derivedFrom":sQuery(id+"F2.wireOp",EDGE,"E1")}),-1.0]])]});
            var Q3;
            Q3=makeQuery(id+"F2.imprint","IMPRINT",FACE,{"disambiguationData":[TD([[makeQuery(id+"F2.imprint","IMPRINT",EDGE,{"derivedFrom":sQuery(id+"F2.wireOp",EDGE,"E37")}),-1.0]])]});
            var Q4;
            Q4=makeQuery(id+"F2.imprint","IMPRINT",FACE,{"disambiguationData":[TD([[makeQuery(id+"F2.imprint","IMPRINT",EDGE,{"derivedFrom":sQuery(id+"F2.wireOp",EDGE,"E96")}),-1.0]])]});
            var Q5;
            Q5=makeQuery(id+"F2.imprint","IMPRINT",FACE,{"disambiguationData":[TD([[makeQuery(id+"F2.imprint","IMPRINT",EDGE,{"derivedFrom":sQuery(id+"F2.wireOp",EDGE,"E204")}),-1.0]])]});
            var Q6;
            Q6=makeQuery(id+"F2.imprint","IMPRINT",FACE,{"disambiguationData":[TD([[makeQuery(id+"F2.imprint","IMPRINT",EDGE,{"derivedFrom":sQuery(id+"F2.wireOp",EDGE,"E296")}),-1.0]])]});
            var Q7;
            Q7=makeQuery(id+"F2.imprint","IMPRINT",FACE,{"disambiguationData":[TD([[makeQuery(id+"F2.imprint","IMPRINT",EDGE,{"derivedFrom":sQuery(id+"F2.wireOp",EDGE,"E360")}),1.0]])]});
            var Q8;
            Q8=makeQuery(id+"F2.imprint","IMPRINT",FACE,{"disambiguationData":[TD([[makeQuery(id+"F2.imprint","IMPRINT",EDGE,{"derivedFrom":sQuery(id+"F2.wireOp",EDGE,"E378")}),1.0]])]});
            var Q9;
            Q9=makeQuery(id+"F2.imprint","IMPRINT",FACE,{"disambiguationData":[TD([[makeQuery(id+"F2.imprint","IMPRINT",EDGE,{"derivedFrom":sQuery(id+"F2.wireOp",EDGE,"E386")}),1.0]])]});
            var Q10;
            Q10=makeQuery(id+"F2.imprint","IMPRINT",FACE,{"disambiguationData":[TD([[makeQuery(id+"F2.imprint","IMPRINT",EDGE,{"derivedFrom":sQuery(id+"F2.wireOp",EDGE,"E396")}),1.0]])]});
            var Q11;
            Q11=makeQuery(id+"F2.imprint","IMPRINT",FACE,{"disambiguationData":[TD([[makeQuery(id+"F2.imprint","IMPRINT",EDGE,{"derivedFrom":sQuery(id+"F2.wireOp",EDGE,"E405")}),1.0]])]});
            var Q12;
            Q12=makeQuery(id+"F2.imprint","IMPRINT",FACE,{"disambiguationData":[TD([[makeQuery(id+"F2.imprint","IMPRINT",EDGE,{"derivedFrom":sQuery(id+"F2.wireOp",EDGE,"E417")}),1.0]])]});
            var Q13;
            Q13=makeQuery(id+"F2.imprint","IMPRINT",FACE,{"disambiguationData":[TD([[makeQuery(id+"F2.imprint","IMPRINT",EDGE,{"derivedFrom":sQuery(id+"F2.wireOp",EDGE,"E375")}),1.0]])]});
            var Q14;
            Q14=makeQuery(id+"F2.imprint","IMPRINT",FACE,{"disambiguationData":[TD([[makeQuery(id+"F2.imprint","IMPRINT",EDGE,{"derivedFrom":sQuery(id+"F2.wireOp",EDGE,"E467")}),-1.0]])]});
            var Q15;
            {var subQ0=sQuery(id+"F2.wireOp",EDGE,"E81");var subQ1=sQuery(id+"F2.wireOp",EDGE,"E26");var subQ2=makeQuery(id+"F2.imprint","INTERSECT",VERTEX,{"derivedFrom":[subQ1,subQ0]});Q15=makeQuery(id+"F2.imprint","IMPRINT",FACE,{"disambiguationData":[TD([[makeQuery(id+"F2.imprint","IMPRINT",EDGE,{"disambiguationData":[TD([[subQ2,1.0]])],"derivedFrom":subQ1}),-1.0]])]});}
            var Q16;
            Q16=makeQuery(id+"F2.imprint","IMPRINT",FACE,{"disambiguationData":[TD([[makeQuery(id+"F2.imprint","IMPRINT",EDGE,{"derivedFrom":sQuery(id+"F2.wireOp",EDGE,"E433")}),-1.0]])]});
            extrude(context, id + "F3", {"entities" : qUnion([Q0, Q1, Q2, Q3, Q4, Q5, Q6, Q7, Q8, Q9, Q10, Q11, Q12, Q13, Q14, Q15, Q16]), "operationType" : NewBodyOperationType.ADD, "depth" : 1.59 * mm, "offsetDistance" : 25.4 * mm});
        }
        {
            var Q0;
            Q0=makeQuery(id+"F1.opExtrude","CAP_EDGE",EDGE,{"disambiguationData":[OSD([sQuery(id+"F0.wireOp",EDGE,"E0.right")])],"isStart":false});
            var Q1;
            Q1=makeQuery(id+"F1.opExtrude","CAP_EDGE",EDGE,{"disambiguationData":[OSD([sQuery(id+"F0.wireOp",EDGE,"E0.top")])],"isStart":false});
            var Q2;
            Q2=makeQuery(id+"F1.opExtrude","CAP_EDGE",EDGE,{"disambiguationData":[OSD([sQuery(id+"F0.wireOp",EDGE,"E0.left")])],"isStart":false});
            var Q3;
            Q3=makeQuery(id+"F1.opExtrude","CAP_EDGE",EDGE,{"disambiguationData":[OSD([sQuery(id+"F0.wireOp",EDGE,"E0.bottom")])],"isStart":false});
            chamfer(context, id + "F4", {"entities" : qUnion([Q0, Q1, Q2, Q3]), "width" : 0.5 * mm, "tangentPropagation" : true});
        }
        {
            var Q0;
            Q0=makeQuery(id+"F1.opExtrude","CAP_EDGE",EDGE,{"disambiguationData":[OSD([sQuery(id+"F0.wireOp",EDGE,"E0.right")])],"isStart":true});
            var Q1;
            Q1=makeQuery(id+"F1.opExtrude","CAP_EDGE",EDGE,{"disambiguationData":[OSD([sQuery(id+"F0.wireOp",EDGE,"E0.bottom")])],"isStart":true});
            var Q2;
            Q2=makeQuery(id+"F1.opExtrude","CAP_EDGE",EDGE,{"disambiguationData":[OSD([sQuery(id+"F0.wireOp",EDGE,"E0.left")])],"isStart":true});
            var Q3;
            Q3=makeQuery(id+"F1.opExtrude","CAP_EDGE",EDGE,{"disambiguationData":[OSD([sQuery(id+"F0.wireOp",EDGE,"E0.top")])],"isStart":true});
            chamfer(context, id + "F5", {"entities" : qUnion([Q0, Q1, Q2, Q3]), "width" : 0.5 * mm, "tangentPropagation" : true});
        }
    });
